# Revit family: Building-ElectricalVehicleCharging-GEWISS-JOINON-ICON_FLUSH-MOUNTING-BOX
name_source: partatom
category: Apparecchi elettrici
units: mm (PartAtom-declared; Revit-internal decimal feet)

## family parameters
Condiviso = No
Host = Superficie
Mantenere orientamento annotazione = Sì
Numero OmniClass = 23.80.30.14.24
Punto di calcolo locali = Sì
Quota connettore circolare = Usa diametro
Taglio con vuoti quando caricato = No
Tipo di parte = Normale
Titolo OmniClass = Junction Boxes

## types (1)
- GWJ8101 - I-CON - FLUSH-MOUNTING BOX
    Bordo = 4 mm  [stored 0.0131234 ft]
    Carico apparente = 0 VA
    Catalogue = E-MOBILITY
    Classificazione = Other
    Description: = I-CON flush-mounting box
    Descrizione = I-CON - FLUSH-MOUNTING BOX
    EAN code = 8034035070815
    Electrocod = 2242
    IDF = 26342d6d-f6c6-4b16-880c-84c37078f428
    IDT = 52568c1f-1458-40a9-8f05-5bfcde2eb16d
    Immagine tipo = ICON_SCATOLA.jpg
    Larghezza = 408 mm
    Lunghezza = 273 mm  [stored 0.895669 ft]
    Modello = GWJ8101
    Produttore = GEWISS S.p.A.
    Profondità = 75 mm
    Prospetto di default = 1219 mm
    Scatola = ROSSO RAL 3000
    Suitable for = WallBox I-CON
    Tappo = GEWISS - BIANCO RAL 9016
    Technical sheet = https://www.gewiss.com
    URL = https://www.gewiss.com
    Version file RFA = 19.4
    Voltaggio = 0 V

note: [stored X ft] marks values corroborated as IEEE doubles in the binary element streams (Revit-internal decimal feet)
